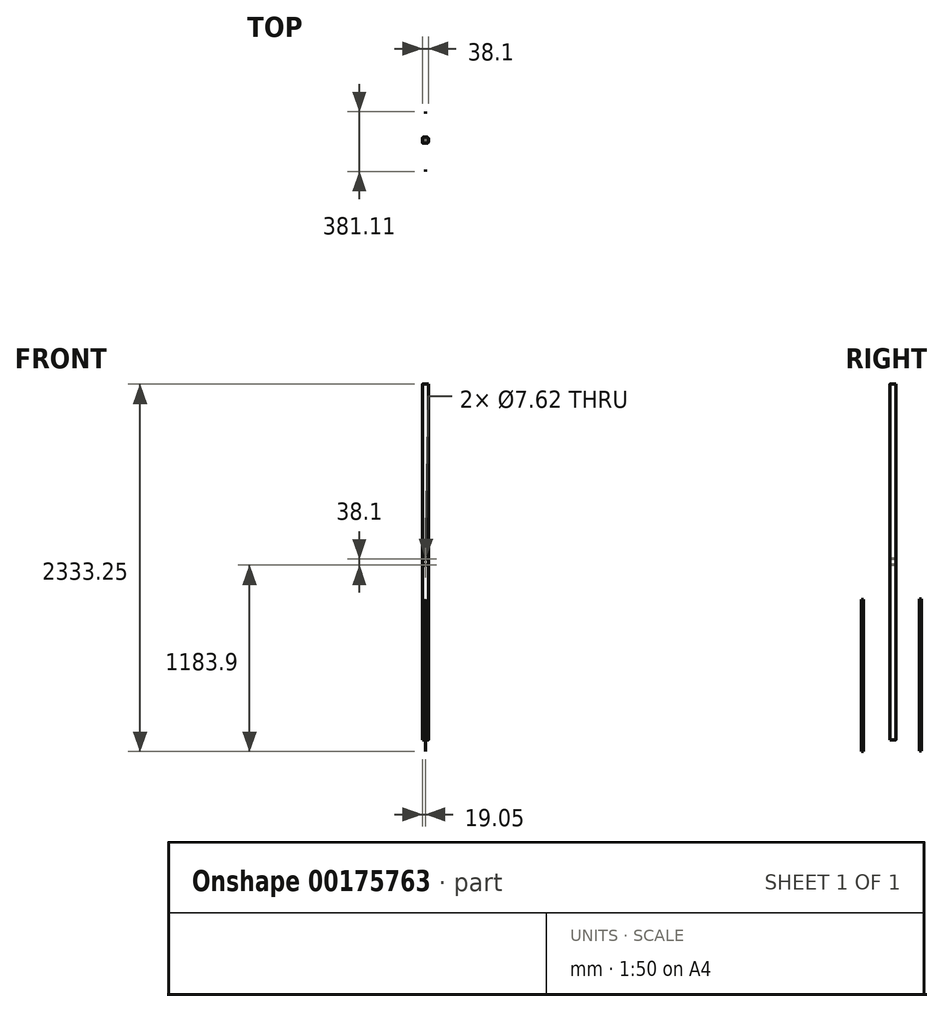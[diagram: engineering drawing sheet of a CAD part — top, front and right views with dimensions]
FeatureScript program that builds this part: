
annotation { "Feature Type Name" : "Feature", "Feature Type Description" : "" }
export const myFeature = defineFeature(function(context is Context, id is Id, definition is map)
    precondition{}
    {
        {
            var Q0;
            Q0=qCreatedBy(makeId("Top.planeOp"),FACE);
            var sketch = newSketch(context, id + "F0", { "sketchPlane" : qUnion([Q0])});
            skLineSegment(sketch, "E0.bottom", {"start": v(12.7, 19.05) * mm, "end": v(-12.7, 19.05) * mm});
            skLineSegment(sketch, "E0.top", {"start": v(12.7, -19.05) * mm, "end": v(-12.7, -19.05) * mm});
            skLineSegment(sketch, "E0.left", {"start": v(19.05, 12.7) * mm, "end": v(19.05, -12.7) * mm});
            skLineSegment(sketch, "E0.right", {"start": v(-19.05, 12.7) * mm, "end": v(-19.05, -12.7) * mm});
            skPoint(sketch, "E0.middle", {"position": v(0, 0) * mm});
            skPoint(sketch, "E1.visualSharp", {"position": v(-19.05, 19.05) * mm});
            skArc(sketch, "E1.filletArc", {"start": v(-12.7, 19.05) * mm, "mid": v(-17.2, 17.2) * mm, "end": v(-19.05, 12.7) * mm});
            skPoint(sketch, "E2.visualSharp", {"position": v(19.05, 19.05) * mm});
            skArc(sketch, "E2.filletArc", {"start": v(19.05, 12.7) * mm, "mid": v(17.2, 17.2) * mm, "end": v(12.7, 19.05) * mm});
            skPoint(sketch, "E3.visualSharp", {"position": v(19.05, -19.05) * mm});
            skArc(sketch, "E3.filletArc", {"start": v(12.7, -19.05) * mm, "mid": v(17.2, -17.2) * mm, "end": v(19.05, -12.7) * mm});
            skPoint(sketch, "E4.visualSharp", {"position": v(-19.05, -19.05) * mm});
            skArc(sketch, "E4.filletArc", {"start": v(-19.05, -12.7) * mm, "mid": v(-17.2, -17.2) * mm, "end": v(-12.7, -19.05) * mm});
            skSolve(sketch);
        }
        {
            var Q0;
            Q0=qSketchRegion(id+"F0",true);
            extrude(context, id + "F1", {"entities" : qUnion([Q0]), "depth" : 2260.6 * mm});
        }
        {
            var Q0;
            Q0=qCreatedBy(makeId("Right.planeOp"),FACE);
            var sketch = newSketch(context, id + "F2", { "sketchPlane" : qUnion([Q0])});
            skLineSegment(sketch, "E5.bottom", {"start": v(-186.2, -72.65) * mm, "end": v(-198.9, -72.65) * mm});
            skLineSegment(sketch, "E5.top", {"start": v(-186.2, 892.55) * mm, "end": v(-198.9, 892.55) * mm});
            skLineSegment(sketch, "E5.left", {"start": v(-186.2, -72.65) * mm, "end": v(-186.2, 892.55) * mm});
            skLineSegment(sketch, "E5.right", {"start": v(-198.9, -72.65) * mm, "end": v(-198.9, 892.55) * mm});
            skPoint(sketch, "E5.middle", {"position": v(-192.55, 409.95) * mm});
            skSolve(sketch);
        }
        {
            var Q0;
            Q0=qCreatedBy(makeId("Right.planeOp"),FACE);
            var sketch = newSketch(context, id + "F3", { "sketchPlane" : qUnion([Q0])});
            skLineSegment(sketch, "E6.bottom", {"start": v(182.21, -70.47) * mm, "end": v(169.51, -70.47) * mm});
            skLineSegment(sketch, "E6.top", {"start": v(182.21, 894.73) * mm, "end": v(169.51, 894.73) * mm});
            skLineSegment(sketch, "E6.left", {"start": v(182.21, -70.47) * mm, "end": v(182.21, 894.73) * mm});
            skLineSegment(sketch, "E6.right", {"start": v(169.51, -70.47) * mm, "end": v(169.51, 894.73) * mm});
            skPoint(sketch, "E6.middle", {"position": v(175.86, 412.13) * mm});
            skSolve(sketch);
        }
        {
            var Q0;
            Q0=makeQuery(id+"F2.imprint","IMPRINT",FACE,{"disambiguationData":[TD([[makeQuery(id+"F2.imprint","IMPRINT",EDGE,{"derivedFrom":sQuery(id+"F2.wireOp",EDGE,"E5.bottom")}),-1.0]])]});
            extrude(context, id + "F4", {"entities" : qUnion([Q0]), "depth" : 0.25 * mm});
        }
        {
            var Q0;
            Q0=makeQuery(id+"F3.imprint","IMPRINT",FACE,{"disambiguationData":[TD([[makeQuery(id+"F3.imprint","IMPRINT",EDGE,{"derivedFrom":sQuery(id+"F3.wireOp",EDGE,"E6.bottom")}),-1.0]])]});
            extrude(context, id + "F5", {"entities" : qUnion([Q0]), "depth" : 0.25 * mm});
        }
        {
            var Q0;
            Q0=makeQuery(id+"F1.opExtrude","SWEPT_FACE",FACE,{"disambiguationData":[OSD([sQuery(id+"F0.wireOp",EDGE,"E0.top")])]});
            var sketch = newSketch(context, id + "F6", { "sketchPlane" : qUnion([Q0])});
            skLineSegment(sketch, "E7", {"start": v(0, 0) * mm, "end": v(0, 1130.3) * mm});
            skLineSegment(sketch, "E8", {"start": v(0, 1130.3) * mm, "end": v(0, 1111.25) * mm});
            skLineSegment(sketch, "E9", {"start": v(0, 1111.25) * mm, "end": v(0, 1149.35) * mm});
            skCircle(sketch, "E10", {"center": v(0, 1111.25) * mm, "radius": 3.81 * mm});
            skCircle(sketch, "E11", {"center": v(0, 1149.35) * mm, "radius": 3.81 * mm});
            skSolve(sketch);
        }
        {
            var Q0;
            Q0 = qSketchRegion(id + "F6", true);
            extrude(context, id + "F7", {"entities" : qUnion([Q0]), "operationType" : NewBodyOperationType.REMOVE, "oppositeDirection" : true, "depth" : 38.1 * mm});
        }
    });
